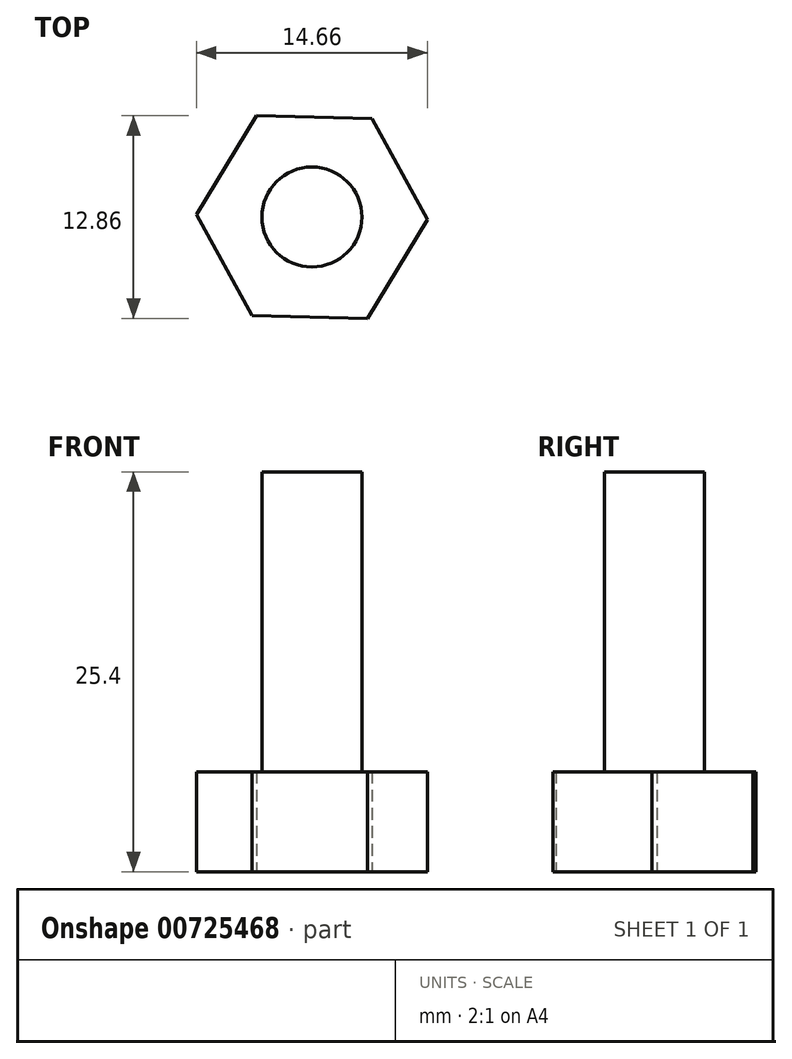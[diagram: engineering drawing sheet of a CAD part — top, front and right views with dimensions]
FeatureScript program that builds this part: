
annotation { "Feature Type Name" : "Feature", "Feature Type Description" : "" }
export const myFeature = defineFeature(function(context is Context, id is Id, definition is map)
    precondition{}
    {
        {
            var Q0;
            Q0=qCreatedBy(makeId("Top.planeOp"),FACE);
            var sketch = newSketch(context, id + "F0", { "sketchPlane" : qUnion([Q0])});
            skCircle(sketch, "E0", {"center": v(0, 0) * mm, "radius": 3.17 * mm});
            skCircle(sketch, "E1.cCircle", {"center": v(0, 0) * mm, "radius": 6.35 * mm, "construction": true});
            skLineSegment(sketch, "E1.0", {"start": v(7.33, -0.17) * mm, "end": v(3.52, -6.43) * mm});
            skLineSegment(sketch, "E1.1", {"start": v(3.52, -6.43) * mm, "end": v(-3.81, -6.26) * mm});
            skLineSegment(sketch, "E1.2", {"start": v(-3.81, -6.26) * mm, "end": v(-7.33, 0.17) * mm});
            skLineSegment(sketch, "E1.3", {"start": v(-7.33, 0.17) * mm, "end": v(-3.52, 6.43) * mm});
            skLineSegment(sketch, "E1.4", {"start": v(-3.52, 6.43) * mm, "end": v(3.81, 6.26) * mm});
            skLineSegment(sketch, "E1.5", {"start": v(3.81, 6.26) * mm, "end": v(7.33, -0.17) * mm});
            skPoint(sketch, "E1.0.midPoint", {"position": v(5.42, -3.3) * mm});
            skSolve(sketch);
        }
        {
            var Q0;
            Q0=makeQuery(id+"F0.imprint","IMPRINT",FACE,{"disambiguationData":[TD([[makeQuery(id+"F0.imprint","IMPRINT",EDGE,{"derivedFrom":sQuery(id+"F0.wireOp",EDGE,"E0")}),1.0]])]});
            extrude(context, id + "F1", {"entities" : qUnion([Q0]), "depth" : 25.4 * mm, "offsetDistance" : 25.4 * mm});
        }
        {
            var Q0;
            Q0=makeQuery(id+"F0.imprint","IMPRINT",FACE,{"disambiguationData":[TD([[makeQuery(id+"F0.imprint","IMPRINT",EDGE,{"derivedFrom":sQuery(id+"F0.wireOp",EDGE,"E0")}),-1.0]])]});
            extrude(context, id + "F2", {"entities" : qUnion([Q0]), "operationType" : NewBodyOperationType.ADD, "depth" : 6.35 * mm, "offsetDistance" : 25.4 * mm});
        }
    });
